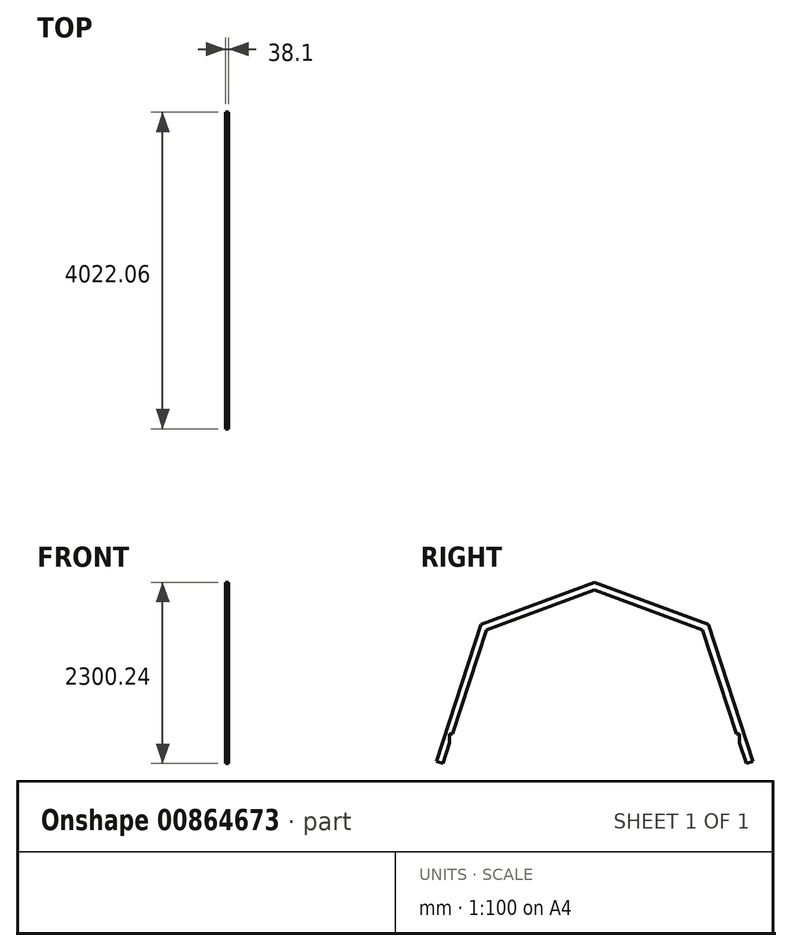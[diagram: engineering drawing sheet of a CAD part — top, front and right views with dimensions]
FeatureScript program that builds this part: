
annotation { "Feature Type Name" : "Feature", "Feature Type Description" : "" }
export const myFeature = defineFeature(function(context is Context, id is Id, definition is map)
    precondition{}
    {
        {
            var Q0;
            Q0=qCreatedBy(makeId("Right.planeOp"),FACE);
            var sketch = newSketch(context, id + "F0", { "sketchPlane" : qUnion([Q0])});
            skLineSegment(sketch, "E0", {"start": v(-1803.4, 0) * mm, "end": v(0, 0) * mm, "construction": true});
            skLineSegment(sketch, "E1", {"start": v(0, 0) * mm, "end": v(0, 1828.8) * mm, "construction": true});
            skPoint(sketch, "E2", {"position": v(-1371.6, 1320.8) * mm});
            skLineSegment(sketch, "E3", {"start": v(0, 1828.8) * mm, "end": v(-1371.6, 1320.8) * mm});
            skLineSegment(sketch, "E4", {"start": v(-1371.6, 1320.8) * mm, "end": v(-1926.53, -376.64) * mm, "construction": true});
            skLineSegment(sketch, "E5", {"start": v(-1926.53, -376.64) * mm, "end": v(-2011.03, -349.02) * mm});
            skLineSegment(sketch, "E6", {"start": v(-2011.03, -349.02) * mm, "end": v(-1442.75, 1389.25) * mm});
            skLineSegment(sketch, "E7", {"start": v(-1442.75, 1389.25) * mm, "end": v(0, 1923.6) * mm});
            skLineSegment(sketch, "E8", {"start": v(0, 1923.6) * mm, "end": v(0, 1828.8) * mm});
            skLineSegment(sketch, "E9.MirrorCS", {"start": v(1442.75, 1389.25) * mm, "end": v(0, 1923.6) * mm});
            skLineSegment(sketch, "E10.MirrorCS", {"start": v(0, 1828.8) * mm, "end": v(1371.6, 1320.8) * mm});
            skLineSegment(sketch, "E11.MirrorCS", {"start": v(2011.03, -349.02) * mm, "end": v(1442.75, 1389.25) * mm});
            skLineSegment(sketch, "E12.MirrorCS", {"start": v(1371.6, 1320.8) * mm, "end": v(1926.53, -376.64) * mm});
            skLineSegment(sketch, "E13.MirrorCS", {"start": v(1926.53, -376.64) * mm, "end": v(2011.03, -349.02) * mm});
            skLineSegment(sketch, "E14.MirrorCS", {"start": v(1803.4, 0) * mm, "end": v(0, 0) * mm, "construction": true});
            skLineSegment(sketch, "E15", {"start": v(-1803.4, 0) * mm, "end": v(-1841.5, 0) * mm});
            skLineSegment(sketch, "E16", {"start": v(-1841.5, 0) * mm, "end": v(-1841.5, -116.54) * mm});
            skLineSegment(sketch, "E17", {"start": v(-1371.6, 1320.8) * mm, "end": v(-1803.4, 0) * mm});
            skLineSegment(sketch, "E18", {"start": v(-1841.5, -116.54) * mm, "end": v(-1926.53, -376.64) * mm});
            skLineSegment(sketch, "E19.MirrorCS", {"start": v(1371.6, 1320.8) * mm, "end": v(1926.53, -376.64) * mm, "construction": true});
            skLineSegment(sketch, "E20.MirrorCS", {"start": v(1841.5, 0) * mm, "end": v(1841.5, -116.54) * mm});
            skLineSegment(sketch, "E21.MirrorCS", {"start": v(1803.4, 0) * mm, "end": v(1841.5, 0) * mm});
            skSolve(sketch);
        }
        {
            var Q0;
            Q0=makeQuery(id+"F0.imprint","IMPRINT",FACE,{"disambiguationData":[TD([[makeQuery(id+"F0.imprint","IMPRINT",EDGE,{"derivedFrom":sQuery(id+"F0.wireOp",EDGE,"E8")}),1.0]])]});
            var Q1;
            Q1=makeQuery(id+"F0.imprint","IMPRINT",FACE,{"disambiguationData":[TD([[makeQuery(id+"F0.imprint","IMPRINT",EDGE,{"derivedFrom":sQuery(id+"F0.wireOp",EDGE,"E3")}),-1.0]])]});
            extrude(context, id + "F1", {"entities" : qUnion([Q0, Q1]), "depth" : 38.1 * mm, "offsetDistance" : 25.4 * mm});
        }
    });
